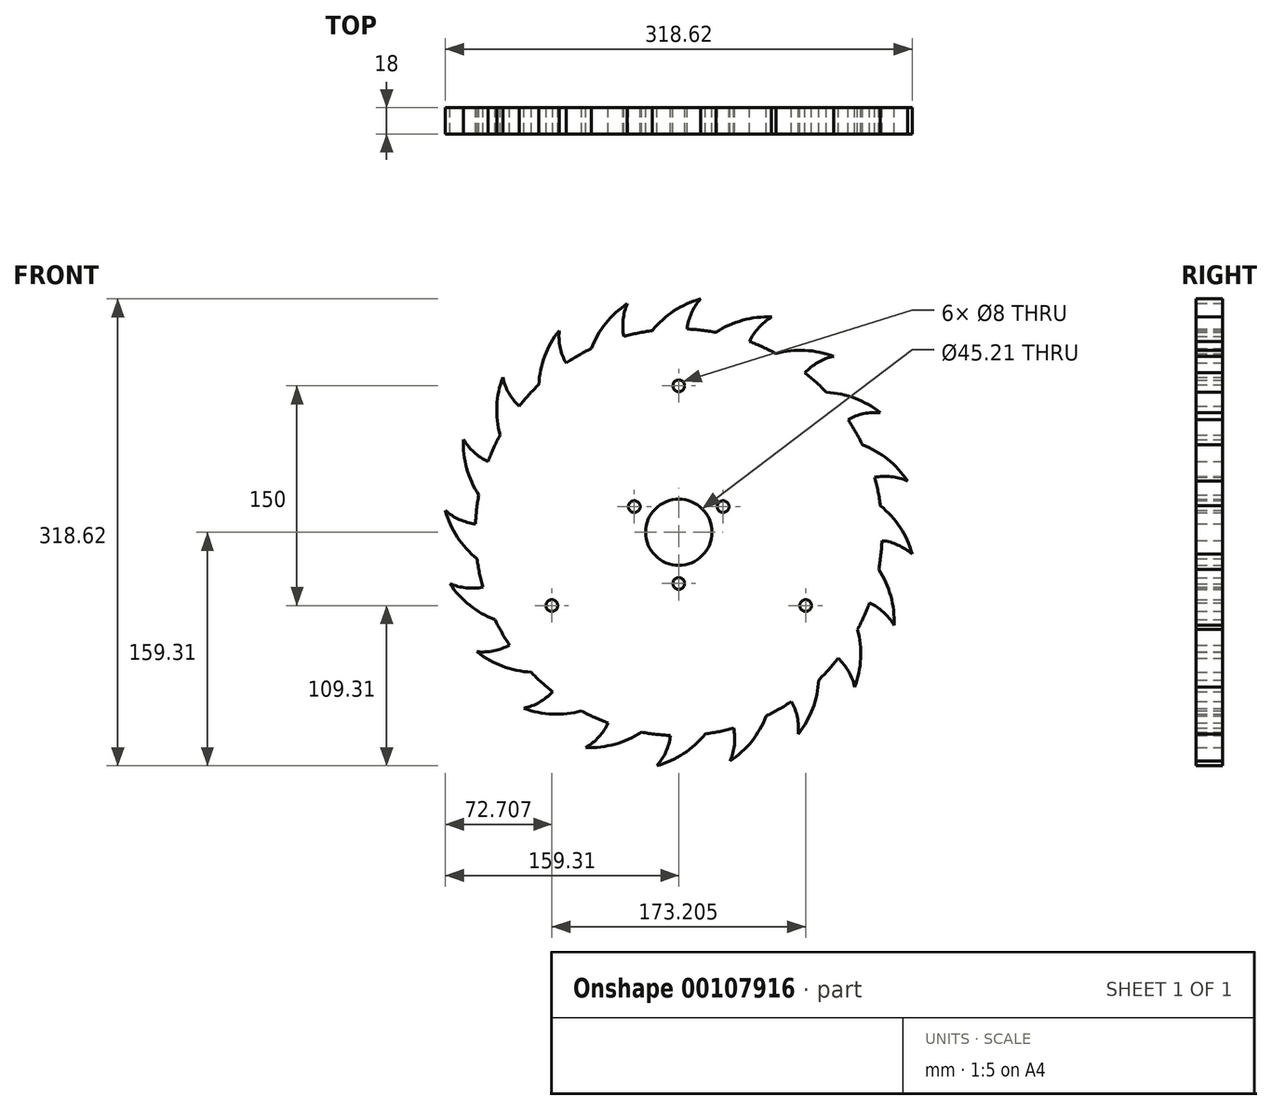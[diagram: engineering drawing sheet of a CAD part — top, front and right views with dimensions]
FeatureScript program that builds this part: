
annotation { "Feature Type Name" : "Feature", "Feature Type Description" : "" }
export const myFeature = defineFeature(function(context is Context, id is Id, definition is map)
    precondition{}
    {
        {
            var Q0;
            Q0=qCreatedBy(makeId("Front.planeOp"),FACE);
            var sketch = newSketch(context, id + "F0", { "sketchPlane" : qUnion([Q0])});
            skCircle(sketch, "E0", {"center": v(0, -35) * mm, "radius": 4 * mm});
            skCircle(sketch, "E1", {"center": v(0, 0) * mm, "radius": 22.6 * mm});
            skCircle(sketch, "E2", {"center": v(0, 100) * mm, "radius": 4 * mm});
            skCircle(sketch, "E3", {"center": v(0, 0) * mm, "radius": 138.84 * mm});
            skCircle(sketch, "E4", {"center": v(0, 0) * mm, "radius": 160 * mm, "construction": true});
            skArc(sketch, "E5", {"start": v(35.09, -156.1) * mm, "mid": v(37.98, -145.08) * mm, "end": v(37.49, -133.68) * mm});
            skArc(sketch, "E6", {"start": v(35.09, -156.1) * mm, "mid": v(49.82, -142.68) * mm, "end": v(59.7, -125.35) * mm});
            skPoint(sketch, "E7", {"position": v(35.09, -156.1) * mm});
            skArc(sketch, "E8.1.0", {"start": v(81.61, -137.62) * mm, "mid": v(80.95, -126.24) * mm, "end": v(76.96, -115.56) * mm});
            skArc(sketch, "E8.1.1", {"start": v(81.61, -137.62) * mm, "mid": v(91.47, -120.3) * mm, "end": v(95.5, -100.77) * mm});
            skArc(sketch, "E8.2.0", {"start": v(120.14, -105.67) * mm, "mid": v(116, -95.04) * mm, "end": v(108.9, -86.12) * mm});
            skArc(sketch, "E8.2.1", {"start": v(120.14, -105.67) * mm, "mid": v(124.17, -86.14) * mm, "end": v(121.97, -66.33) * mm});
            skArc(sketch, "E8.3.0", {"start": v(146.92, -63.37) * mm, "mid": v(139.7, -54.55) * mm, "end": v(130.19, -48.25) * mm});
            skArc(sketch, "E8.3.1", {"start": v(146.92, -63.37) * mm, "mid": v(144.71, -43.56) * mm, "end": v(136.5, -25.4) * mm});
            skArc(sketch, "E8.4.0", {"start": v(159.3, -14.87) * mm, "mid": v(149.71, -8.7) * mm, "end": v(138.73, -5.66) * mm});
            skArc(sketch, "E8.4.1", {"start": v(159.3, -14.87) * mm, "mid": v(151.09, 3.3) * mm, "end": v(137.67, 18.03) * mm});
            skArc(sketch, "E8.5.0", {"start": v(156.1, 35.09) * mm, "mid": v(145.08, 37.98) * mm, "end": v(133.68, 37.49) * mm});
            skArc(sketch, "E8.5.1", {"start": v(156.1, 35.09) * mm, "mid": v(142.68, 49.82) * mm, "end": v(125.35, 59.7) * mm});
            skArc(sketch, "E8.6.0", {"start": v(137.62, 81.61) * mm, "mid": v(126.24, 80.95) * mm, "end": v(115.56, 76.96) * mm});
            skArc(sketch, "E8.6.1", {"start": v(137.62, 81.61) * mm, "mid": v(120.3, 91.47) * mm, "end": v(100.77, 95.5) * mm});
            skArc(sketch, "E8.7.0", {"start": v(105.67, 120.14) * mm, "mid": v(95.04, 116) * mm, "end": v(86.12, 108.9) * mm});
            skArc(sketch, "E8.7.1", {"start": v(105.67, 120.14) * mm, "mid": v(86.14, 124.17) * mm, "end": v(66.33, 121.97) * mm});
            skArc(sketch, "E8.8.0", {"start": v(63.37, 146.92) * mm, "mid": v(54.55, 139.7) * mm, "end": v(48.25, 130.19) * mm});
            skArc(sketch, "E8.8.1", {"start": v(63.37, 146.92) * mm, "mid": v(43.56, 144.71) * mm, "end": v(25.4, 136.5) * mm});
            skArc(sketch, "E8.9.0", {"start": v(14.87, 159.3) * mm, "mid": v(8.7, 149.71) * mm, "end": v(5.66, 138.73) * mm});
            skArc(sketch, "E8.9.1", {"start": v(14.87, 159.3) * mm, "mid": v(-3.3, 151.09) * mm, "end": v(-18.03, 137.67) * mm});
            skArc(sketch, "E8.10.0", {"start": v(-35.09, 156.1) * mm, "mid": v(-37.98, 145.08) * mm, "end": v(-37.49, 133.68) * mm});
            skArc(sketch, "E8.10.1", {"start": v(-35.09, 156.1) * mm, "mid": v(-49.82, 142.68) * mm, "end": v(-59.7, 125.35) * mm});
            skArc(sketch, "E8.11.0", {"start": v(-81.61, 137.62) * mm, "mid": v(-80.95, 126.24) * mm, "end": v(-76.96, 115.56) * mm});
            skArc(sketch, "E8.11.1", {"start": v(-81.61, 137.62) * mm, "mid": v(-91.47, 120.3) * mm, "end": v(-95.5, 100.77) * mm});
            skArc(sketch, "E8.12.0", {"start": v(-120.14, 105.67) * mm, "mid": v(-116, 95.04) * mm, "end": v(-108.9, 86.12) * mm});
            skArc(sketch, "E8.12.1", {"start": v(-120.14, 105.67) * mm, "mid": v(-124.17, 86.14) * mm, "end": v(-121.97, 66.33) * mm});
            skArc(sketch, "E8.13.0", {"start": v(-146.92, 63.37) * mm, "mid": v(-139.7, 54.55) * mm, "end": v(-130.19, 48.25) * mm});
            skArc(sketch, "E8.13.1", {"start": v(-146.92, 63.37) * mm, "mid": v(-144.71, 43.56) * mm, "end": v(-136.5, 25.4) * mm});
            skArc(sketch, "E8.14.0", {"start": v(-159.3, 14.87) * mm, "mid": v(-149.71, 8.7) * mm, "end": v(-138.73, 5.66) * mm});
            skArc(sketch, "E8.14.1", {"start": v(-159.3, 14.87) * mm, "mid": v(-151.09, -3.3) * mm, "end": v(-137.67, -18.03) * mm});
            skCircle(sketch, "E9.1.0", {"center": v(30.31, 17.5) * mm, "radius": 4 * mm});
            skCircle(sketch, "E9.2.0", {"center": v(-30.31, 17.5) * mm, "radius": 4 * mm});
            skCircle(sketch, "E10.1.0", {"center": v(-86.6, -50) * mm, "radius": 4 * mm});
            skCircle(sketch, "E10.2.0", {"center": v(86.6, -50) * mm, "radius": 4 * mm});
            skArc(sketch, "E11.1.15.0", {"start": v(-156.1, -35.09) * mm, "mid": v(-145.08, -37.98) * mm, "end": v(-133.68, -37.49) * mm});
            skArc(sketch, "E11.4.15.0", {"start": v(-156.1, -35.09) * mm, "mid": v(-142.68, -49.82) * mm, "end": v(-125.35, -59.7) * mm});
            skArc(sketch, "E11.1.16.0", {"start": v(-137.62, -81.61) * mm, "mid": v(-126.24, -80.95) * mm, "end": v(-115.56, -76.96) * mm});
            skArc(sketch, "E11.4.16.0", {"start": v(-137.62, -81.61) * mm, "mid": v(-120.3, -91.47) * mm, "end": v(-100.77, -95.5) * mm});
            skArc(sketch, "E12.1.17.0", {"start": v(-105.67, -120.14) * mm, "mid": v(-95.04, -116) * mm, "end": v(-86.12, -108.9) * mm});
            skArc(sketch, "E12.4.17.0", {"start": v(-105.67, -120.14) * mm, "mid": v(-86.14, -124.17) * mm, "end": v(-66.33, -121.97) * mm});
            skArc(sketch, "E12.1.18.0", {"start": v(-63.37, -146.92) * mm, "mid": v(-54.55, -139.7) * mm, "end": v(-48.25, -130.19) * mm});
            skArc(sketch, "E12.4.18.0", {"start": v(-63.37, -146.92) * mm, "mid": v(-43.56, -144.71) * mm, "end": v(-25.4, -136.5) * mm});
            skArc(sketch, "E12.1.19.0", {"start": v(-14.87, -159.3) * mm, "mid": v(-8.7, -149.71) * mm, "end": v(-5.66, -138.73) * mm});
            skArc(sketch, "E12.4.19.0", {"start": v(-14.87, -159.3) * mm, "mid": v(3.3, -151.09) * mm, "end": v(18.03, -137.67) * mm});
            skCircle(sketch, "E13", {"center": v(0, 0) * mm, "radius": 150 * mm, "construction": true});
            skSolve(sketch);
        }
        {
            var Q0;
            Q0=makeQuery(id+"F0.imprint","IMPRINT",FACE,{"disambiguationData":[TD([[makeQuery(id+"F0.imprint","IMPRINT",EDGE,{"derivedFrom":sQuery(id+"F0.wireOp",EDGE,"E0")}),-1.0]])]});
            var Q1;
            {var subQ0=sQuery(id+"F0.wireOp",EDGE,"E8.14.0");Q1=makeQuery(id+"F0.imprint","IMPRINT",FACE,{"disambiguationData":[TD([[makeQuery(id+"F0.imprint","IMPRINT",EDGE,{"derivedFrom":subQ0}),-1.0]])]});}
            var Q2;
            {var subQ0=sQuery(id+"F0.wireOp",EDGE,"E8.13.0");Q2=makeQuery(id+"F0.imprint","IMPRINT",FACE,{"disambiguationData":[TD([[makeQuery(id+"F0.imprint","IMPRINT",EDGE,{"derivedFrom":subQ0}),-1.0]])]});}
            var Q3;
            {var subQ0=sQuery(id+"F0.wireOp",EDGE,"E8.12.0");Q3=makeQuery(id+"F0.imprint","IMPRINT",FACE,{"disambiguationData":[TD([[makeQuery(id+"F0.imprint","IMPRINT",EDGE,{"derivedFrom":subQ0}),-1.0]])]});}
            var Q4;
            {var subQ0=sQuery(id+"F0.wireOp",EDGE,"E8.11.0");Q4=makeQuery(id+"F0.imprint","IMPRINT",FACE,{"disambiguationData":[TD([[makeQuery(id+"F0.imprint","IMPRINT",EDGE,{"derivedFrom":subQ0}),-1.0]])]});}
            var Q5;
            {var subQ0=sQuery(id+"F0.wireOp",EDGE,"E8.10.0");Q5=makeQuery(id+"F0.imprint","IMPRINT",FACE,{"disambiguationData":[TD([[makeQuery(id+"F0.imprint","IMPRINT",EDGE,{"derivedFrom":subQ0}),-1.0]])]});}
            var Q6;
            {var subQ0=sQuery(id+"F0.wireOp",EDGE,"E8.9.0");Q6=makeQuery(id+"F0.imprint","IMPRINT",FACE,{"disambiguationData":[TD([[makeQuery(id+"F0.imprint","IMPRINT",EDGE,{"derivedFrom":subQ0}),-1.0]])]});}
            var Q7;
            {var subQ0=sQuery(id+"F0.wireOp",EDGE,"E8.8.0");Q7=makeQuery(id+"F0.imprint","IMPRINT",FACE,{"disambiguationData":[TD([[makeQuery(id+"F0.imprint","IMPRINT",EDGE,{"derivedFrom":subQ0}),-1.0]])]});}
            var Q8;
            {var subQ0=sQuery(id+"F0.wireOp",EDGE,"E8.7.0");Q8=makeQuery(id+"F0.imprint","IMPRINT",FACE,{"disambiguationData":[TD([[makeQuery(id+"F0.imprint","IMPRINT",EDGE,{"derivedFrom":subQ0}),-1.0]])]});}
            var Q9;
            {var subQ0=sQuery(id+"F0.wireOp",EDGE,"E8.6.0");Q9=makeQuery(id+"F0.imprint","IMPRINT",FACE,{"disambiguationData":[TD([[makeQuery(id+"F0.imprint","IMPRINT",EDGE,{"derivedFrom":subQ0}),-1.0]])]});}
            var Q10;
            {var subQ0=sQuery(id+"F0.wireOp",EDGE,"E8.5.0");Q10=makeQuery(id+"F0.imprint","IMPRINT",FACE,{"disambiguationData":[TD([[makeQuery(id+"F0.imprint","IMPRINT",EDGE,{"derivedFrom":subQ0}),-1.0]])]});}
            var Q11;
            {var subQ0=sQuery(id+"F0.wireOp",EDGE,"E8.4.0");Q11=makeQuery(id+"F0.imprint","IMPRINT",FACE,{"disambiguationData":[TD([[makeQuery(id+"F0.imprint","IMPRINT",EDGE,{"derivedFrom":subQ0}),-1.0]])]});}
            var Q12;
            {var subQ0=sQuery(id+"F0.wireOp",EDGE,"E8.3.0");Q12=makeQuery(id+"F0.imprint","IMPRINT",FACE,{"disambiguationData":[TD([[makeQuery(id+"F0.imprint","IMPRINT",EDGE,{"derivedFrom":subQ0}),-1.0]])]});}
            var Q13;
            {var subQ0=sQuery(id+"F0.wireOp",EDGE,"E8.2.0");Q13=makeQuery(id+"F0.imprint","IMPRINT",FACE,{"disambiguationData":[TD([[makeQuery(id+"F0.imprint","IMPRINT",EDGE,{"derivedFrom":subQ0}),-1.0]])]});}
            var Q14;
            {var subQ0=sQuery(id+"F0.wireOp",EDGE,"E8.1.0");Q14=makeQuery(id+"F0.imprint","IMPRINT",FACE,{"disambiguationData":[TD([[makeQuery(id+"F0.imprint","IMPRINT",EDGE,{"derivedFrom":subQ0}),-1.0]])]});}
            var Q15;
            {var subQ0=sQuery(id+"F0.wireOp",EDGE,"E5");Q15=makeQuery(id+"F0.imprint","IMPRINT",FACE,{"disambiguationData":[TD([[makeQuery(id+"F0.imprint","IMPRINT",EDGE,{"derivedFrom":subQ0}),-1.0]])]});}
            var Q16;
            {var subQ0=sQuery(id+"F0.wireOp",EDGE,"E12.1.19.0");Q16=makeQuery(id+"F0.imprint","IMPRINT",FACE,{"disambiguationData":[TD([[makeQuery(id+"F0.imprint","IMPRINT",EDGE,{"derivedFrom":subQ0}),-1.0]])]});}
            var Q17;
            {var subQ0=sQuery(id+"F0.wireOp",EDGE,"E12.1.18.0");Q17=makeQuery(id+"F0.imprint","IMPRINT",FACE,{"disambiguationData":[TD([[makeQuery(id+"F0.imprint","IMPRINT",EDGE,{"derivedFrom":subQ0}),-1.0]])]});}
            var Q18;
            {var subQ0=sQuery(id+"F0.wireOp",EDGE,"E12.1.17.0");Q18=makeQuery(id+"F0.imprint","IMPRINT",FACE,{"disambiguationData":[TD([[makeQuery(id+"F0.imprint","IMPRINT",EDGE,{"derivedFrom":subQ0}),-1.0]])]});}
            var Q19;
            {var subQ0=sQuery(id+"F0.wireOp",EDGE,"E11.1.16.0");Q19=makeQuery(id+"F0.imprint","IMPRINT",FACE,{"disambiguationData":[TD([[makeQuery(id+"F0.imprint","IMPRINT",EDGE,{"derivedFrom":subQ0}),-1.0]])]});}
            var Q20;
            {var subQ0=sQuery(id+"F0.wireOp",EDGE,"E11.1.15.0");Q20=makeQuery(id+"F0.imprint","IMPRINT",FACE,{"disambiguationData":[TD([[makeQuery(id+"F0.imprint","IMPRINT",EDGE,{"derivedFrom":subQ0}),-1.0]])]});}
            extrude(context, id + "F1", {"entities" : qUnion([Q0, Q1, Q2, Q3, Q4, Q5, Q6, Q7, Q8, Q9, Q10, Q11, Q12, Q13, Q14, Q15, Q16, Q17, Q18, Q19, Q20]), "depth" : 18 * mm, "offsetDistance" : 25 * mm});
        }
    });
